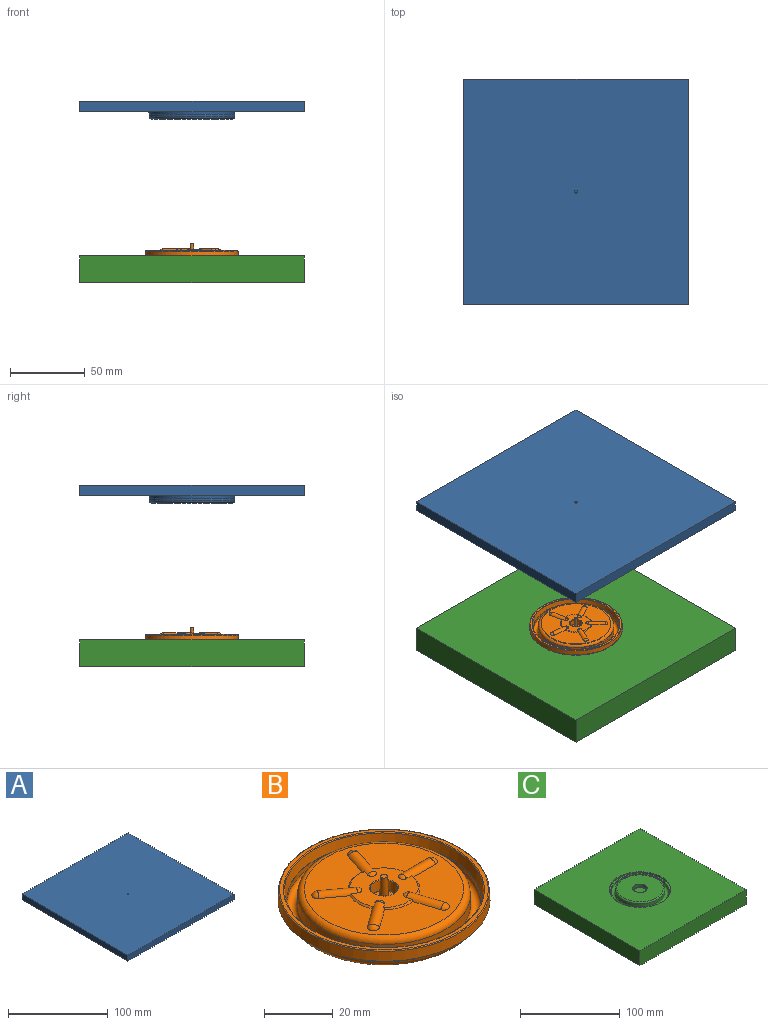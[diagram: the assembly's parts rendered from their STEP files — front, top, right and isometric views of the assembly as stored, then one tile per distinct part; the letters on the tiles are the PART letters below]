
ASSEMBLY  parts=3 mates=3
PART A: 44 faces, bbox 150x150x12 mm
  f0: torus R=29.25mm, axis (0,0,-1), area 23.8mm2, adj f1,f2
  f1: cone r=28.46mm half-angle=9.5deg, axis (0,0,1), area 619.7mm2, adj f0,f40
  f2: cylinder r=28.45mm len=56.9mm, axis (0,0,-1), area 276.5mm2, adj f0,f3
  f3: torus R=26.86mm, axis (0,0,-1), area 838.1mm2, adj f2,f4
  f4: cone r=25.23mm half-angle=0.7deg, axis (0,0,-1), area 568.1mm2, adj f3,f5
  f5: torus R=23.23mm, axis (0,0,-1), area 479.5mm2, adj f4,f6
  f6: plane 46.46x46.46mm, normal (0,0,-1), area 1162mm2, adj f5,f7,f10,f11,f12,f13,f14,f15
  f7: cylinder r=2mm len=12.03mm, axis (-0.31,-0.95,0), area 48.1mm2, adj f6,f9,f10,f11,f23,f28
  f8: torus R=4.24mm, axis (0,0,-1), area 7.7mm2, adj f9,f30
  f9: plane 20x19.9mm, normal (0,0,-1), area 214mm2, adj f7,f8,f11,f12,f14,f15,f17,f18
  f10: sphere r=2mm, area 6.9mm2, adj f6,f7
  f11: cone r=10mm half-angle=45deg, axis (0,0,-1), area 6.8mm2, adj f6,f7,f9,f12
  f12: cylinder r=2mm len=11.39mm, axis (0.81,-0.59,0), area 48.1mm2, adj f6,f9,f11,f13,f14,f27
  f13: sphere r=2mm, area 6.9mm2, adj f6,f12
  f14: cone r=10mm half-angle=45deg, axis (0,0,-1), area 6.8mm2, adj f6,f9,f12,f15
  f15: cylinder r=2mm len=11.39mm, axis (0.81,0.59,0), area 48.1mm2, adj f6,f9,f14,f16,f17,f26
  f16: sphere r=2mm, area 6.9mm2, adj f6,f15
  f17: cone r=10mm half-angle=45deg, axis (0,0,-1), area 6.8mm2, adj f6,f9,f15,f18
  f18: cylinder r=2mm len=12.03mm, axis (-0.31,0.95,0), area 48.1mm2, adj f6,f9,f17,f19,f20,f25
  f19: sphere r=2mm, area 6.9mm2, adj f6,f18
  f20: cone r=10mm half-angle=45deg, axis (0,0,-1), area 6.8mm2, adj f6,f9,f18,f21
  f21: cylinder r=2mm len=11.49mm, axis (-1,0,0), area 48.1mm2, adj f6,f9,f20,f22,f23,f24
  f22: sphere r=2mm, area 6.9mm2, adj f6,f21
  f23: cone r=10mm half-angle=45deg, axis (0,0,-1), area 6.8mm2, adj f6,f7,f9,f21
  f24: sphere r=2mm, area 3.8mm2, adj f9,f21
  f25: sphere r=2mm, area 3.8mm2, adj f9,f18
  f26: sphere r=2mm, area 3.8mm2, adj f9,f15
  f27: sphere r=2mm, area 3.8mm2, adj f9,f12
  f28: sphere r=2mm, area 3.8mm2, adj f7,f9
  f29: plane 2x2mm, normal (0,0,-1), area 3.1mm2, adj f32
  f30: cone r=3.75mm half-angle=5deg, axis (0,0,1), area 81.9mm2, adj f8,f31
  f31: torus R=3.55mm, axis (0,0,-1), area 6.8mm2, adj f30,f33
  f32: cone r=1.27mm half-angle=2deg, axis (0,0,-1), area 55.7mm2, adj f29,f33
  f33: plane 7.1x7.1mm, normal (0,0,-1), area 34.5mm2, adj f31,f32
  f34: plane 150x7mm, normal (0,1,0), area 1050mm2, adj f35,f37,f38,f39
  f35: plane 150x7mm, normal (-1,0,0), area 1050mm2, adj f34,f36,f38,f39
  f36: plane 150x7mm, normal (0,-1,0), area 1050mm2, adj f35,f37,f38,f39
  f37: plane 150x7mm, normal (1,0,0), area 1050mm2, adj f34,f36,f38,f39
  f38: plane 150x150mm, normal (0,0,1), area 22500mm2, adj f34,f35,f36,f37
  f39: plane 150x150mm, normal (0,0,-1), area 19509mm2, adj f34,f35,f36,f37,f43
  f40: torus R=29.33mm, axis (0,0,-1), area 77.2mm2, adj f1,f41
  f41: plane 60.94x60.94mm, normal (0,0,-1), area 215.3mm2, adj f40,f42
  f42: torus R=30.47mm, axis (0,0,-1), area 87.8mm2, adj f41,f43
  f43: cone r=30.77mm half-angle=3deg, axis (0,0,-1), area 313.2mm2, adj f39,f42
PART B: 49 faces, bbox 66.6x66.6x12.2 mm
  f0: cylinder r=7.25mm len=14.5mm, axis (0,0,-1), area 143.4mm2, adj f21,f22
  f1: cone r=10mm half-angle=45deg, axis (0,0,-1), area 6.8mm2, adj f3,f29,f32,f45
  f2: cone r=10mm half-angle=45deg, axis (0,0,-1), area 6.8mm2, adj f3,f29,f42,f45
  f3: plane 46.46x46.46mm, normal (0,0,1), area 1162mm2, adj f1,f2,f4,f5,f6,f30,f32,f33
  f4: cone r=10mm half-angle=45deg, axis (0,0,-1), area 6.8mm2, adj f3,f29,f39,f42
  f5: cone r=10mm half-angle=45deg, axis (0,0,-1), area 6.8mm2, adj f3,f29,f36,f39
  f6: cone r=10mm half-angle=45deg, axis (0,0,-1), area 6.8mm2, adj f3,f29,f32,f36
  f7: torus R=26.86mm, axis (0,0,-1), area 838.1mm2, adj f8,f31
  f8: cylinder r=28.45mm len=56.9mm, axis (0,0,-1), area 276.5mm2, adj f7,f9
  f9: torus R=29.25mm, axis (0,0,-1), area 23.8mm2, adj f8,f10
  f10: cone r=28.46mm half-angle=9.5deg, axis (0,0,1), area 619.7mm2, adj f9,f11
  f11: torus R=29.33mm, axis (0,0,-1), area 77.2mm2, adj f10,f12
  f12: plane 60.94x60.94mm, normal (0,0,1), area 215.3mm2, adj f11,f13
  f13: torus R=30.47mm, axis (0,0,-1), area 87.8mm2, adj f12,f14
  f14: cone r=30.77mm half-angle=3deg, axis (0,0,-1), area 663.2mm2, adj f13,f15
  f15: plane 61.9x61.9mm, normal (0,0,-1), area 321.5mm2, adj f14,f16
  f16: torus R=29.25mm, axis (0,0,-1), area 86mm2, adj f15,f17
  f17: cylinder r=28.95mm len=57.9mm, axis (0,0,-1), area 238.9mm2, adj f16,f18
  f18: torus R=26.86mm, axis (0,0,-1), area 1102.3mm2, adj f17,f19
  f19: cone r=24.78mm half-angle=0.7deg, axis (0,0,-1), area 556.9mm2, adj f18,f20
  f20: torus R=23.23mm, axis (0,0,-1), area 355mm2, adj f19,f21
  f21: plane 46.46x46.46mm, normal (0,0,-1), area 1530.2mm2, adj f0,f20
  f22: cone r=7.25mm half-angle=30deg, axis (0,0,-1), area 69.2mm2, adj f0,f23
  f23: torus R=7.8mm, axis (0,0,-1), area 20.9mm2, adj f22,f24
  f24: plane 15.6x15.6mm, normal (0,0,-1), area 191.1mm2, adj f23
  f25: plane 7.1x7.1mm, normal (0,0,1), area 34.5mm2, adj f26,f47
  f26: torus R=3.55mm, axis (0,0,-1), area 6.8mm2, adj f25,f27
  f27: cone r=3.75mm half-angle=5deg, axis (0,0,1), area 81.9mm2, adj f26,f28
  f28: torus R=4.24mm, axis (0,0,-1), area 7.7mm2, adj f27,f29
  f29: plane 20x19.9mm, normal (0,0,1), area 214mm2, adj f1,f2,f4,f5,f6,f28,f32,f34
  f30: torus R=23.23mm, axis (0,0,-1), area 479.5mm2, adj f3,f31
  f31: cone r=25.23mm half-angle=0.7deg, axis (0,0,-1), area 568.1mm2, adj f7,f30
  f32: cylinder r=2mm len=11.49mm, axis (-1,0,0), area 48.1mm2, adj f1,f3,f6,f29,f33,f34
  f33: sphere r=2mm, area 6.9mm2, adj f3,f32
  f34: sphere r=2mm, area 3.8mm2, adj f29,f32
  f35: sphere r=2mm, area 3.8mm2, adj f29,f36
  f36: cylinder r=2mm len=12.03mm, axis (-0.31,0.95,0), area 48.1mm2, adj f3,f5,f6,f29,f35,f37
  f37: sphere r=2mm, area 6.9mm2, adj f3,f36
  f38: sphere r=2mm, area 3.8mm2, adj f29,f39
  f39: cylinder r=2mm len=11.39mm, axis (0.81,0.59,0), area 48.1mm2, adj f3,f4,f5,f29,f38,f40
  f40: sphere r=2mm, area 6.9mm2, adj f3,f39
  f41: sphere r=2mm, area 3.8mm2, adj f29,f42
  f42: cylinder r=2mm len=11.39mm, axis (0.81,-0.59,0), area 48.1mm2, adj f2,f3,f4,f29,f41,f43
  f43: sphere r=2mm, area 6.9mm2, adj f3,f42
  f44: sphere r=2mm, area 3.8mm2, adj f29,f45
  f45: cylinder r=2mm len=12.03mm, axis (-0.31,-0.95,0), area 48.1mm2, adj f1,f2,f3,f29,f44,f46
  f46: sphere r=2mm, area 6.9mm2, adj f3,f45
  f47: cone r=1.27mm half-angle=2deg, axis (0,0,-1), area 55.7mm2, adj f25,f48
  f48: plane 2x2mm, normal (0,0,1), area 3.1mm2, adj f47
PART C: 18 faces, bbox 150x150x19.6 mm
  f0: torus R=23.23mm, axis (0,0,-1), area 355mm2, adj f1,f2
  f1: cone r=24.78mm half-angle=0.7deg, axis (0,0,-1), area 556.9mm2, adj f0,f8
  f2: plane 46.46x46.46mm, normal (0,0,1), area 1530.2mm2, adj f0,f3
  f3: cylinder r=7.25mm len=14.5mm, axis (0,0,-1), area 143.4mm2, adj f2,f6
  f4: plane 15.6x15.6mm, normal (0,0,1), area 191.1mm2, adj f5
  f5: torus R=7.8mm, axis (0,0,-1), area 20.9mm2, adj f4,f6
  f6: cone r=7.25mm half-angle=30deg, axis (0,0,-1), area 69.2mm2, adj f3,f5
  f7: cylinder r=28.95mm len=57.9mm, axis (0,0,-1), area 238.9mm2, adj f8,f9
  f8: torus R=26.86mm, axis (0,0,-1), area 1102.3mm2, adj f1,f7
  f9: torus R=29.25mm, axis (0,0,-1), area 86mm2, adj f7,f10
  f10: plane 61.9x61.9mm, normal (0,0,1), area 321.5mm2, adj f9,f11
  f11: cone r=30.77mm half-angle=3deg, axis (0,0,-1), area 350mm2, adj f10,f12
  f12: plane 150x150mm, normal (0,0,1), area 19509mm2, adj f11,f14,f15,f16,f17
  f13: plane 150x150mm, normal (0,0,-1), area 22500mm2, adj f14,f15,f16,f17
  f14: plane 150x18mm, normal (1,0,0), area 2700mm2, adj f12,f13,f15,f17
  f15: plane 150x18mm, normal (0,-1,0), area 2700mm2, adj f12,f13,f14,f16
  f16: plane 150x18mm, normal (-1,0,0), area 2700mm2, adj f12,f13,f15,f17
  f17: plane 150x18mm, normal (0,1,0), area 2700mm2, adj f12,f13,f14,f16
PLACE A rot(axis=(0,0,1),0deg) t=(-0.26,1.44,75.9)mm fixed
PLACE B rot(axis=(0,0,1),28.2deg) t=(-0.26,1.44,-18.75)mm
PLACE C t=(-0.26,1.44,-20.33)mm
MATE planar A.f35 <-> C.f16  axis (-1,0,0) through (-75.26,1.44,84.9)mm
MATE revolute B.f0 <-> C.f0  axis (0,0,-1) through (-0.26,1.44,-13.21)mm
MATE planar A.f36 <-> C.f15  axis (0,-1,0) through (-0.26,-73.56,84.9)mm
